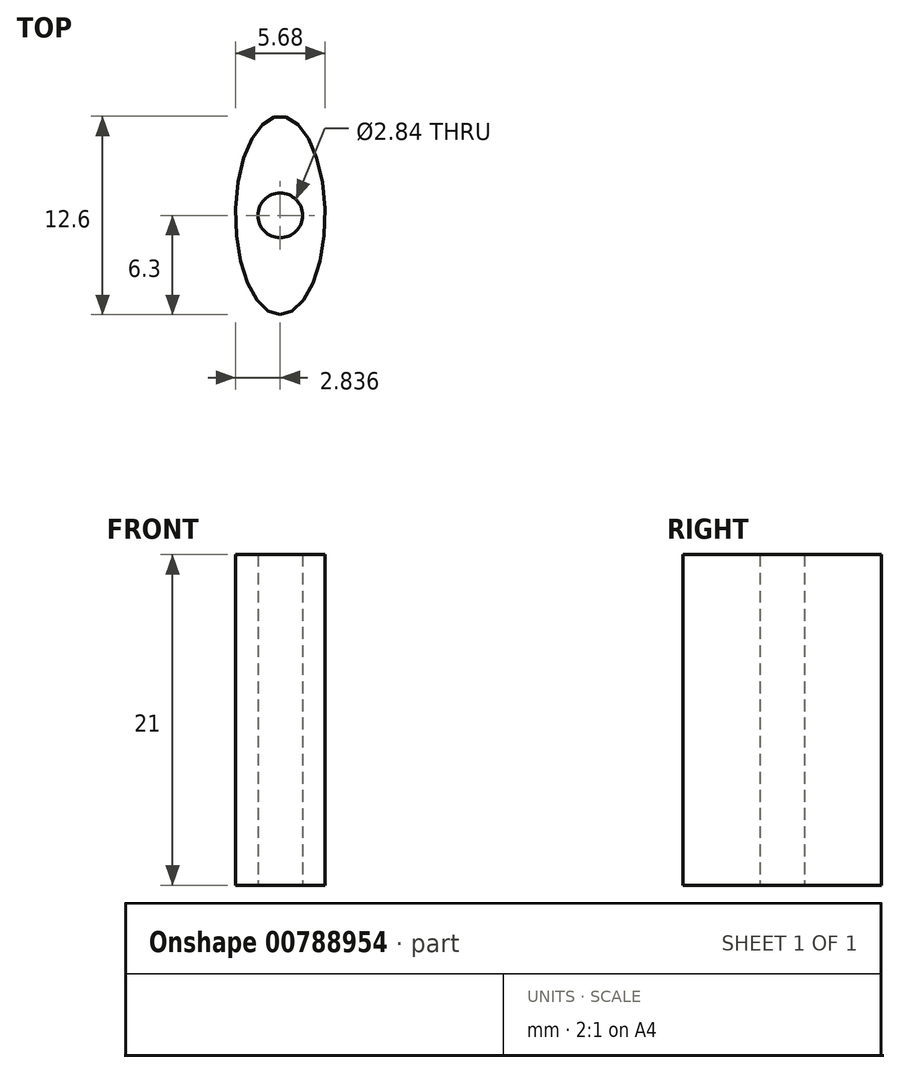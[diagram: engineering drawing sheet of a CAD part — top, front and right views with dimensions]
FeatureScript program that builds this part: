
annotation { "Feature Type Name" : "Feature", "Feature Type Description" : "" }
export const myFeature = defineFeature(function(context is Context, id is Id, definition is map)
    precondition{}
    {
        {
            var Q0;
            Q0=qCreatedBy(makeId("Top.planeOp"),FACE);
            var sketch = newSketch(context, id + "F0", { "sketchPlane" : qUnion([Q0])});
            skEllipse(sketch, "E0", {"center": v(14.17, 0) * mm, "majorRadius": 2.84 * mm, "minorRadius": 6.3 * mm, "majorAxis": v(-1, 0)});
            skCircle(sketch, "E1", {"center": v(14.17, 0) * mm, "radius": 1.42 * mm});
            skSolve(sketch);
        }
        {
            var Q0;
            Q0=makeQuery(id+"F0.imprint","IMPRINT",FACE,{"disambiguationData":[TD([[makeQuery(id+"F0.imprint","IMPRINT",EDGE,{"derivedFrom":sQuery(id+"F0.wireOp",EDGE,"E0")}),1.0]])]});
            extrude(context, id + "F1", {"entities" : qUnion([Q0]), "depth" : 21 * mm, "offsetDistance" : 25 * mm});
        }
    });
